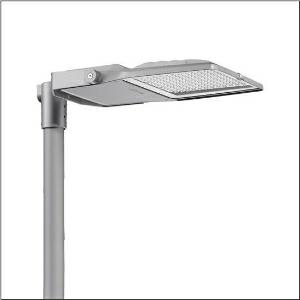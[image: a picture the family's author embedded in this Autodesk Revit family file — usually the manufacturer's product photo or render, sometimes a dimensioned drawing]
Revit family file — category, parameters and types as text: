
# Revit family: floodlight_fl_21_midi___pl43_5xa7786e2a3a_b253
name_source: partatom
category: Lighting Fixtures
units: mm (PartAtom-declared; Revit-internal decimal feet)

## family parameters
Cut with Voids When Loaded = No
Host = Face
Light Source = No
Part Type = Normal
Room Calculation Point = No
Round Connector Dimension = Use Diameter
Shared = No

## types (1)
- --- (1 x LED, 27640 lm, 212.4 W, 3000K)
    Apparent Load = 212 VA
    CIE Flux Codes = 27 78 99 100 100
    Color Rendering = 70
    Color Temperature = 3000K
    Default Elevation = 1800 mm
    Description = Floodlight FL 21 midi, floodlight, primary light control with lens, of PMMA, primary optical cover: protective disc, of toughened safety glass, transparent, light distribution: PL43, light emission: direct distribution, installation type: surface-mounted, LED, High Power LED, rated luminous flux: 27.640lm, luminous efficacy: 130lm/W, light colour: 730, colour temperature: 3000K, control gear: Smart Interface (Zhaga), control: flexible luminous flux parameterisation, time-dependent luminous flux control, constant luminous flux control, overheat protection, pre-setting: logarithmic dimming characteristic, with terminal, 6-pole, mains connection: 220..240V, AC, 50/60Hz, start of lifetime: 212W, end of service life: 231W, reduction: 95W, luminaire housing, of diecast aluminium, powder-coated, SITECO metallic grey (DB 702S), corrosivity category C5 mid according to DIN EN ISO 12944, suitable for swimming pools, chlorine-resistant, sealing non-destructively replaceable, please order mast flange separately, mast bracket, of steel, galvanised, powder-coated, SITECO metallic grey (DB 702S), Smart Interface below and above, protection rating (complete): IP66, insulation class (complete): insulation class II (safety insulation), certification: CE, ENEC, VDE, protection symbol: D, impact resistance: IK08, permissible operating ambient temperature: -40..+40°C, permissible operating ambient temperature for outdoor applications: -40..+50°C, standard: DIN EN 12944, LABS conformity tested according to VDMA 24364:2018-05, packaging unit: 1 piece

Light Distribution: PL43
    Height = 76 mm
    Lamp = 1 x LED
    Lamp Light Flux = 27640 lm
    Lamp Power = 212.4 W
    Lamp count = 1
    Length = 657 mm
    Luminous efficacy = 130 lm/W
    Manufacturer = Siteco
    ModVariant = No
    Model = 5XA7786E2A3A
    Number of Poles = 1
    OnlyDefault = Yes
    Power Factor = 1
    Product Name = Floodlight FL 21 midi | PL43
    Product group = floodlight | pylon annexe
    ProductGroupID = 6201
    Protection Class = Protection class II
    Protection Degree = IP 66
    RLX_Detail_Level = 1
    RLX_Emergency_Light_Flux = 0 lm
    RLX_Emergency_Type = 0
    RLX_Emergency_Type_DB = No
    RlxData = <blob elided: 153485 chars, md5=eab5781c>
    Socket = socket
    Standby Power = 0 W
    System Light Flux = 27640 lm
    System Power = 212 W
    Type Comments = factory setting: luminous flux: 100 % | dim-lin: 254 | 710 mA
    Type Image = l_1007123.jpg
    URL = http://relux.com
    VarID = @adj_176731
    Voltage = 0 V
    Weight = 0.00 kg
    Width = 442 mm

## geometry (parser evidence)
native form markers: Blend x4, Sweep x16
no freeform markers — native parametric forms only
